FCSTD DOCUMENT  (FreeCAD 0.21R33694 (Git))
Label: WR90step
License: All rights reserved
LicenseURL: http://en.wikipedia.org/wiki/All_rights_reserved
objects: Part::Part2DObjectPython×2, App::FeaturePython×1
note: 2 computed .brp shape members not serialized (recipe doc carries the construction recipe); baked Part::Feature solids carry a one-line shape summary decoded from their .brp

FEATURE [Part::Part2DObjectPython] Rectangle  label="rectangle"  # Draft 2D object (typed FeaturePython)
  Area = 0.000277978
  ChamferSize = 0
  Columns = 1
  FilletRadius = 0
  Height = 0.01216
  Length = 0.02286
  MakeFace = true
  Placement = pos=(-37.2684,-90.4864,0) rot=(0,0,1;0rad)
  Rows = 1
FEATURE [App::FeaturePython] Text  label="_M1(voltage){v1}"  # WARN: FeaturePython — macro-defined, semantics opaque (R4)
  Placement = pos=(-37.2383,-90.4803,0) rot=(0,0,1;0rad)
  Text = .
FEATURE [Part::Part2DObjectPython] Line  label="_Pv1"  # Draft 2D object (typed FeaturePython)
  Area = 0
  ChamferSize = 0
  Closed = false
  End = (-37.2569,-90.4743,0)
  FilletRadius = 0
  Length = 0.01216
  MakeFace = true
  Placement = pos=(-37.2569,-90.4864,0) rot=(0,0,1;0rad)
  Points = (2) [(0,0,0),(0,0.01216,0)]
  Start = (-37.2569,-90.4864,0)
  Subdivisions = 0
